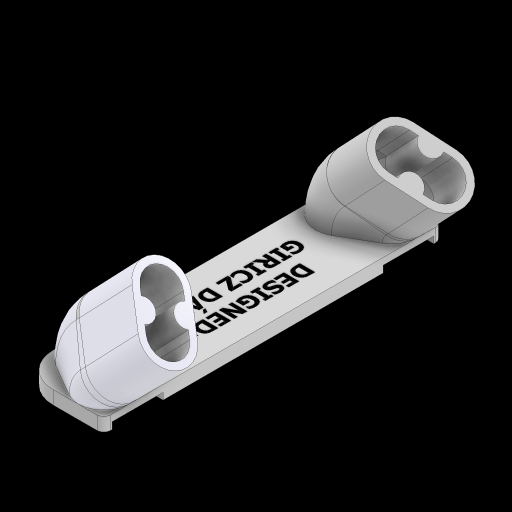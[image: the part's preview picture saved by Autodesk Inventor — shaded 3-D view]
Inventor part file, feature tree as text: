
AUTODESK INVENTOR PART (.ipt)
format: ipt  version: 2023 (Build 270158000, 158)  size: 978,944 bytes
history: native  units: mm
features: extrude x17, sketch x12, plane x2, revolve x2, chamfer x2, fillet x2, sweep x1, mirror x1
ambient origin geometry x8: Origin, YZ Plane, XZ Plane, XY Plane, X Axis, Y Axis, Z Axis, Center Point
bodies: Solid1 (feature_tree)
feature tree (39):
  sketch  "Sketch1"  dims[d0=100.0mm d1=25.0mm d2=7.5mm d3=7.5mm d4=60.0deg d5=15.0mm d6=11.0mm d7=11.0mm d8=15.0mm d11=135.0deg]
  plane  "Work Plane1"
  sweep  "Sweep1"
  extrude  "Extrusion1"  Depth=4.0mm TaperAngle=0.0deg
  revolve  "Revolution1"  Angle=45.0deg
  sketch  "Sketch6"  dims[d31=10.0mm d32=45.0deg]
  extrude  "Extrusion4"  TaperAngle=45.0deg  [1 undecoded]
  extrude  "Extrusion5"  Depth=10.0mm
  sketch  "Sketch7"  dims[d33=10.0mm d34=10.0mm]
  extrude  "Extrusion6"  Depth=10.0mm
  extrude  "Extrusion7"  Depth=15.0mm
  mirror  "Mirror4"
  plane  "Work Plane9"
  extrude  "Extrusion8"  Depth=5.5mm
  revolve  "Revolution2"  [1 undecoded]
  extrude  "Extrusion9"  Depth=6.5mm
  sketch  "Sketch19"  dims[d60=5.5mm d61=5.5mm]
  extrude  "Extrusion10"  Depth=20.0mm TaperAngle=0.0deg
  extrude  "Extrusion11"  Depth=10.0mm
  extrude  "Extrusion12"  TaperAngle=90.0deg  [1 undecoded]
  sketch  "Sketch21"  dims[d65=2.0mm d66=6.5mm]
  extrude  "Extrusion13"  Depth=10.0mm
  chamfer  "Chamfer3"  Distance=5.5mm
  extrude  "Extrusion15"  Depth=10.0mm
  extrude  "Extrusion18"  Depth=10.0mm
  fillet  "Fillet2"  Radius=11.0mm
  fillet  "Fillet3"  Radius=11.0mm
  extrude  "Extrusion19"  Depth=10.0mm
  extrude  "Extrusion20"  Depth=10.0mm
  extrude  "Extrusion21"  Depth=10.0mm
  extrude  "Extrusion22"  Depth=10.0mm TaperAngle=0.0deg
  chamfer  "Chamfer5"  Distance=10.0mm
  sketch  "Sketch3"  dims[d12=0.0mm d13=0.0mm d14=4.0mm d15=0.0mm]
  sketch  "Sketch5"  dims[d29=11.389087mm d30=45.0deg]
  sketch  "Sketch14"  dims[d35=45.0deg d37=10.0mm]
  sketch  "Sketch15"  dims[d38=0.977384mm d57=15.0mm]
  sketch  "Sketch20"  dims[d63=11.0mm d64=11.0mm]
  sketch  "Sketch22"  dims[d67=6.5mm d68=20.0mm d69=0.0mm]
  sketch  "Sketch23"  dims[d70=325.0mm d71=0.0mm d72=7.5mm d73=90.0deg d74=7.5mm d75=5.5mm d76=5.5mm d77=15.0mm d78=11.0mm d79=11.0mm d80=2.0mm d81=6.5mm d82=6.5mm d83=10.0mm d84=0.0mm d93=10.0mm d94=0.0mm d115=20.0mm d116=0.0mm d131=8.726646mm d132=300.0mm d133=0.0mm d134=15.0mm d135=300.0mm d136=0.0mm d137=11.0mm d138=11.0mm d139=2.0mm d140=6.5mm d141=6.5mm d142=10.0mm d143=0.0mm d144=40.0mm d145=0.0mm d146=25.0mm d147=100.0mm d150=15.0mm d151=5.5mm d152=2.0mm d153=0.0mm d156=2.0mm d157=4.0mm d158=45.0deg d162=549.891mm d163=50.0mm d164=100.0mm d167=2.5mm d169=15.0mm d170=17.5mm d171=17.5mm d174=10.0mm d175=300.0mm d176=0.0mm d177=7.5mm d183=2.0mm d184=0.0mm d185=2.0mm d186=10.0mm d187=3.0mm d188=0.0mm d189=15.0mm d190=0.0mm d191=1.0mm d192=0.0mm d193=6.5mm d194=10.0mm d195=0.0mm d196=2.0mm d197=4.0mm d198=45.0deg d178=0.872665mm]
note: 3 required parameter values undecoded (feature->parameter linkage not recoverable at this tier; creation-order binding heuristic only, values carry confidence <= 0.55)